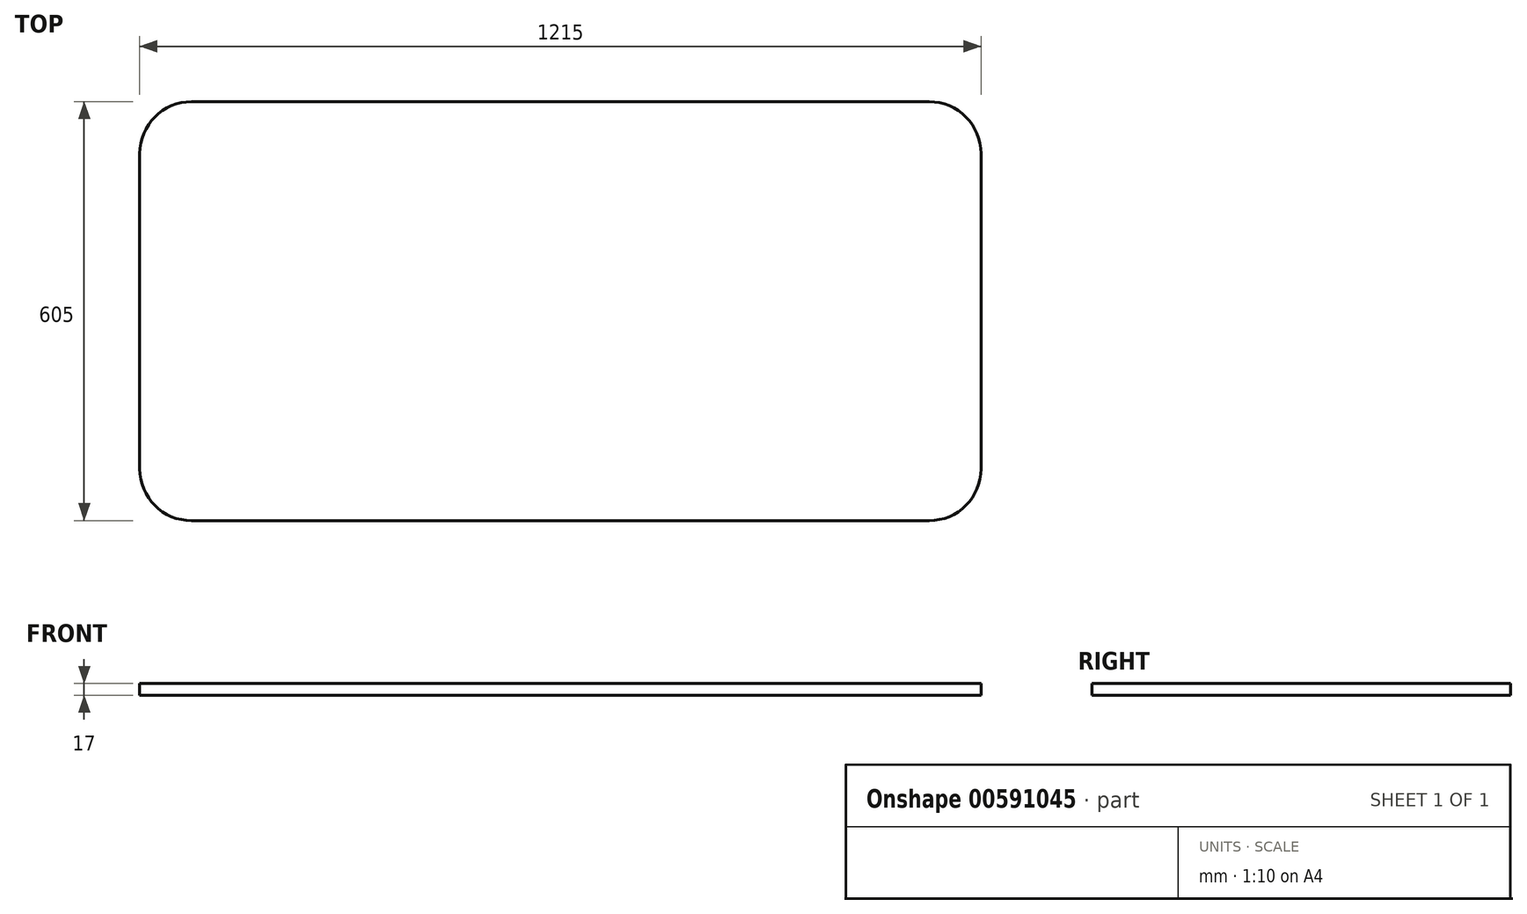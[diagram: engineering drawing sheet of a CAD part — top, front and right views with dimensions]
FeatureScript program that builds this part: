
annotation { "Feature Type Name" : "Feature", "Feature Type Description" : "" }
export const myFeature = defineFeature(function(context is Context, id is Id, definition is map)
    precondition{}
    {
        {
            var Q0;
            Q0=qCreatedBy(makeId("Top.planeOp"),FACE);
            var sketch = newSketch(context, id + "F0", { "sketchPlane" : qUnion([Q0])});
            skLineSegment(sketch, "E0.bottom", {"start": v(532.5, 302.5) * mm, "end": v(-532.5, 302.5) * mm});
            skLineSegment(sketch, "E0.top", {"start": v(532.5, -302.5) * mm, "end": v(-532.5, -302.5) * mm});
            skLineSegment(sketch, "E0.left", {"start": v(607.5, 227.5) * mm, "end": v(607.5, -227.5) * mm});
            skLineSegment(sketch, "E0.right", {"start": v(-607.5, 227.5) * mm, "end": v(-607.5, -227.5) * mm});
            skPoint(sketch, "E0.middle", {"position": v(0, 0) * mm});
            skPoint(sketch, "E1.visualSharp", {"position": v(-607.5, 302.5) * mm});
            skArc(sketch, "E1.filletArc", {"start": v(-532.5, 302.5) * mm, "mid": v(-585.53, 280.53) * mm, "end": v(-607.5, 227.5) * mm});
            skPoint(sketch, "E2.visualSharp", {"position": v(607.5, 302.5) * mm});
            skArc(sketch, "E2.filletArc", {"start": v(607.5, 227.5) * mm, "mid": v(585.53, 280.53) * mm, "end": v(532.5, 302.5) * mm});
            skPoint(sketch, "E3.visualSharp", {"position": v(607.5, -302.5) * mm});
            skArc(sketch, "E3.filletArc", {"start": v(532.5, -302.5) * mm, "mid": v(585.53, -280.53) * mm, "end": v(607.5, -227.5) * mm});
            skPoint(sketch, "E4.visualSharp", {"position": v(-607.5, -302.5) * mm});
            skArc(sketch, "E4.filletArc", {"start": v(-607.5, -227.5) * mm, "mid": v(-585.53, -280.53) * mm, "end": v(-532.5, -302.5) * mm});
            skSolve(sketch);
        }
        {
            var Q0;
            Q0 = qSketchRegion(id + "F0", true);
            extrude(context, id + "F1", {"entities" : qUnion([Q0]), "endBound" : BoundingType.SYMMETRIC, "depth" : 17 * mm, "offsetDistance" : 25 * mm});
        }
    });
